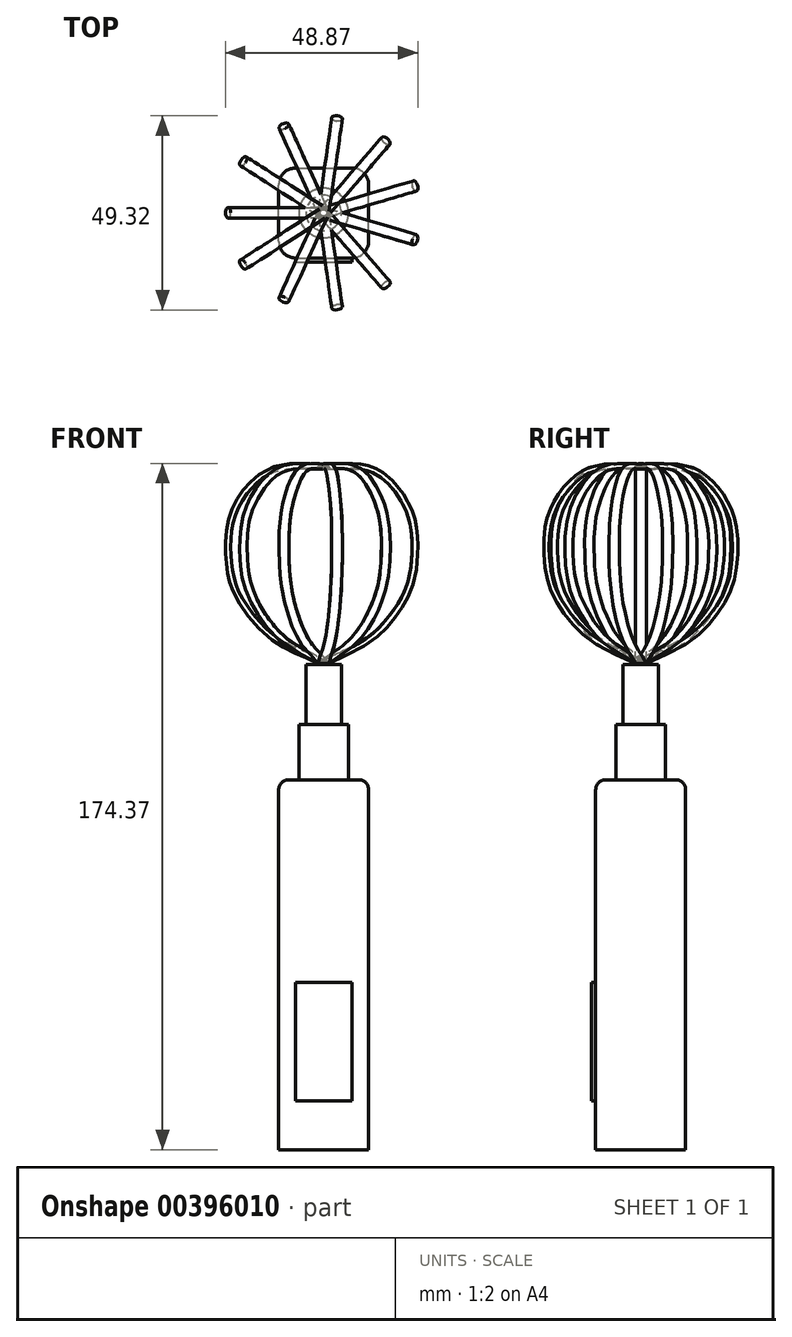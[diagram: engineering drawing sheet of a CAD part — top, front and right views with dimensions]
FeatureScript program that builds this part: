
annotation { "Feature Type Name" : "Feature", "Feature Type Description" : "" }
export const myFeature = defineFeature(function(context is Context, id is Id, definition is map)
    precondition{}
    {
        {
            var Q0;
            Q0=qCreatedBy(makeId("Front.planeOp"),FACE);
            var sketch = newSketch(context, id + "F0", { "sketchPlane" : qUnion([Q0])});
            skLineSegment(sketch, "E0", {"start": v(-13.86, -65.4) * mm, "end": v(-13.86, 28.57) * mm});
            skLineSegment(sketch, "E1", {"start": v(-13.86, 28.57) * mm, "end": v(9, 28.57) * mm});
            skLineSegment(sketch, "E2", {"start": v(9, 28.57) * mm, "end": v(9, -65.4) * mm});
            skLineSegment(sketch, "E3", {"start": v(9, -65.4) * mm, "end": v(-13.86, -65.4) * mm});
            skSolve(sketch);
        }
        {
            var Q0;
            Q0 = qSketchRegion(id + "F0", true);
            extrude(context, id + "F1", {"entities" : qUnion([Q0]), "depth" : 22.86 * mm});
        }
        {
            var Q0;
            Q0=makeQuery(id+"F1.opExtrude","CAP_EDGE",EDGE,{"disambiguationData":[OSD([sQuery(id+"F0.wireOp",EDGE,"E0")])],"isStart":true});
            var Q1;
            Q1=makeQuery(id+"F1.opExtrude","CAP_EDGE",EDGE,{"disambiguationData":[OSD([sQuery(id+"F0.wireOp",EDGE,"E0")])],"isStart":false});
            var Q2;
            Q2=makeQuery(id+"F1.opExtrude","CAP_EDGE",EDGE,{"disambiguationData":[OSD([sQuery(id+"F0.wireOp",EDGE,"E2")])],"isStart":true});
            var Q3;
            Q3=makeQuery(id+"F1.opExtrude","CAP_EDGE",EDGE,{"disambiguationData":[OSD([sQuery(id+"F0.wireOp",EDGE,"E2")])],"isStart":false});
            fillet(context, id + "F2", {"entities" : qUnion([Q0, Q1, Q2, Q3]), "radius" : 4.3 * mm, "tangentPropagation" : true, "allowEdgeOverflow" : false});
        }
        {
            var Q0;
            Q0=makeQuery(id+"F1.opExtrude","CAP_EDGE",EDGE,{"disambiguationData":[OSD([sQuery(id+"F0.wireOp",EDGE,"E1")])],"isStart":false});
            fillet(context, id + "F3", {"entities" : qUnion([Q0]), "radius" : 2.54 * mm, "tangentPropagation" : true, "allowEdgeOverflow" : false});
        }
        {
            var Q0;
            Q0=qCreatedBy(makeId("Top.planeOp"),FACE);
            cPlane(context, id + "F4", {"entities" : qUnion([Q0]), "cplaneType" : CPlaneType.OFFSET, "offset" : 28.45 * mm, "width" : 152.4 * mm, "height" : 152.4 * mm});
        }
        {
            var Q0;
            Q0=qCreatedBy(id+"F4.planeOp",FACE);
            var sketch = newSketch(context, id + "F5", { "sketchPlane" : qUnion([Q0])});
            skCircle(sketch, "E4", {"center": v(-2.43, -11.43) * mm, "radius": 6.3 * mm});
            skSolve(sketch);
        }
        {
            var Q0;
            Q0 = qSketchRegion(id + "F5", true);
            extrude(context, id + "F6", {"entities" : qUnion([Q0]), "operationType" : NewBodyOperationType.ADD, "depth" : 14.22 * mm});
        }
        {
            var Q0;
            Q0=qCreatedBy(id+"F4.planeOp",FACE);
            cPlane(context, id + "F7", {"entities" : qUnion([Q0]), "cplaneType" : CPlaneType.OFFSET, "offset" : 12.45 * mm, "width" : 152.4 * mm, "height" : 152.4 * mm});
        }
        {
            var Q0;
            Q0=qCreatedBy(id+"F7.planeOp",FACE);
            var sketch = newSketch(context, id + "F8", { "sketchPlane" : qUnion([Q0])});
            skCircle(sketch, "E5", {"center": v(-2.43, -11.43) * mm, "radius": 4.51 * mm});
            skSolve(sketch);
        }
        {
            var Q0;
            Q0 = qSketchRegion(id + "F8", true);
            extrude(context, id + "F9", {"entities" : qUnion([Q0]), "operationType" : NewBodyOperationType.ADD, "depth" : 17.02 * mm});
        }
        {
            var Q0;
            Q0=qCreatedBy(makeId("Front.planeOp"),FACE);
            cPlane(context, id + "F10", {"entities" : qUnion([Q0]), "cplaneType" : CPlaneType.OFFSET, "offset" : 23.1 * mm, "width" : 152.4 * mm, "height" : 152.4 * mm});
        }
        {
            var Q0;
            Q0=makeQuery(id+"F1.opExtrude","CAP_FACE",FACE,{"disambiguationData":[OSD([sQuery(id+"F0.wireOp",EDGE,"E0"),sQuery(id+"F0.wireOp",EDGE,"E1"),sQuery(id+"F0.wireOp",EDGE,"E2"),sQuery(id+"F0.wireOp",EDGE,"E3")])],"isStart":false});
            var sketch = newSketch(context, id + "F11", { "sketchPlane" : qUnion([Q0])});
            skLineSegment(sketch, "E6.bottom", {"start": v(-9.56, -53.07) * mm, "end": v(4.71, -53.07) * mm});
            skLineSegment(sketch, "E6.top", {"start": v(-9.56, -22.97) * mm, "end": v(4.71, -22.97) * mm});
            skLineSegment(sketch, "E6.left", {"start": v(-9.56, -53.07) * mm, "end": v(-9.56, -22.97) * mm});
            skLineSegment(sketch, "E6.right", {"start": v(4.71, -53.07) * mm, "end": v(4.71, -22.97) * mm});
            skSolve(sketch);
        }
        {
            var Q0;
            Q0=makeQuery(id+"F11.imprint","IMPRINT",FACE,{"disambiguationData":[TD([[makeQuery(id+"F11.imprint","IMPRINT",EDGE,{"derivedFrom":sQuery(id+"F11.wireOp",EDGE,"E6.bottom")}),1.0]])]});
            extrude(context, id + "F12", {"entities" : qUnion([Q0]), "operationType" : NewBodyOperationType.ADD, "depth" : 1.02 * mm});
        }
        {
            var Q0;
            Q0=makeQuery(id+"F12.opExtrude","CAP_FACE",FACE,{"disambiguationData":[OSD([sQuery(id+"F11.wireOp",EDGE,"E6.bottom"),sQuery(id+"F11.wireOp",EDGE,"E6.top"),sQuery(id+"F11.wireOp",EDGE,"E6.left"),sQuery(id+"F11.wireOp",EDGE,"E6.right")])],"isStart":false});
            var sketch = newSketch(context, id + "F13", { "sketchPlane" : qUnion([Q0])});
            skLineSegment(sketch, "E7", {"start": v(-7.14, -26.06) * mm, "end": v(2.29, -26.06) * mm});
            skSolve(sketch);
        }
        {
            var Q0;
            Q0=sQuery(id+"F13.wireOp",EDGE,"E7");
            extrude(context, id + "F14", {"bodyType" : ToolBodyType.SURFACE, "surfaceEntities" : qUnion([Q0]), "oppositeDirection" : true, "depth" : 2.03 * mm});
        }
        {
            var Q0;
            Q0=makeQuery(id+"F12.opExtrude","CAP_FACE",FACE,{"disambiguationData":[OSD([sQuery(id+"F11.wireOp",EDGE,"E6.bottom"),sQuery(id+"F11.wireOp",EDGE,"E6.top"),sQuery(id+"F11.wireOp",EDGE,"E6.left"),sQuery(id+"F11.wireOp",EDGE,"E6.right")])],"isStart":false});
            var sketch = newSketch(context, id + "F15", { "sketchPlane" : qUnion([Q0])});
            skLineSegment(sketch, "E8", {"start": v(-9.56, -48.5) * mm, "end": v(4.71, -48.5) * mm});
            skLineSegment(sketch, "E9", {"start": v(-9.56, -45.95) * mm, "end": v(4.71, -45.95) * mm});
            skLineSegment(sketch, "E10", {"start": v(-9.56, -41.38) * mm, "end": v(4.71, -41.38) * mm});
            skLineSegment(sketch, "E11", {"start": v(-9.56, -38.84) * mm, "end": v(4.71, -38.84) * mm});
            skSolve(sketch);
        }
        {
            var Q0;
            Q0=sQuery(id+"F15.wireOp",EDGE,"E8");
            extrude(context, id + "F16", {"bodyType" : ToolBodyType.SURFACE, "surfaceEntities" : qUnion([Q0]), "oppositeDirection" : true, "depth" : 5.82 * mm});
        }
        {
            var Q0;
            Q0=sQuery(id+"F15.wireOp",EDGE,"E11");
            var Q1;
            Q1=sQuery(id+"F15.wireOp",EDGE,"E10");
            var Q2;
            Q2=sQuery(id+"F15.wireOp",EDGE,"E9");
            var Q3;
            Q3=sQuery(id+"F15.wireOp",EDGE,"E8");
            extrude(context, id + "F17", {"bodyType" : ToolBodyType.SURFACE, "surfaceEntities" : qUnion([Q0, Q1, Q2, Q3]), "oppositeDirection" : true, "depth" : 9.5 * mm});
        }
        {
            var Q0;
            Q0=qCreatedBy(id+"F10.planeOp",FACE);
            cPlane(context, id + "F18", {"entities" : qUnion([Q0]), "cplaneType" : CPlaneType.OFFSET, "offset" : 11.68 * mm, "oppositeDirection" : true, "width" : 152.4 * mm, "height" : 152.4 * mm});
        }
        {
            var Q0;
            Q0=qCreatedBy(id+"F7.planeOp",FACE);
            cPlane(context, id + "F19", {"entities" : qUnion([Q0]), "cplaneType" : CPlaneType.OFFSET, "offset" : 17.02 * mm, "oppositeDirection" : true, "width" : 152.4 * mm, "height" : 152.4 * mm});
        }
        {
            var Q0;
            Q0=qCreatedBy(id+"F18.planeOp",FACE);
            var sketch = newSketch(context, id + "F20", { "sketchPlane" : qUnion([Q0])});
            skFitSpline(sketch, "E12", {"points": [v(-2.52, 58.13) * mm, v(-14.5, 64.12) * mm, v(-24.33, 75.65) * mm, v(-26.6, 85.02) * mm, v(-25.58, 95.76) * mm, v(-19.59, 104.69) * mm, v(-12.24, 108.08) * mm, v(-2.8, 108.12) * mm], "startDerivative": vector(-79.34, 44.57) * mm, "endDerivative": vector(49.51, -0.45) * mm});
            skSolve(sketch);
        }
        {
            var Q0;
            Q0=makeQuery(id+"F9.opExtrude","CAP_FACE",FACE,{"disambiguationData":[OSD([sQuery(id+"F8.wireOp",EDGE,"E5")])],"isStart":false});
            cPlane(context, id + "F21", {"entities" : qUnion([Q0]), "cplaneType" : CPlaneType.OFFSET, "offset" : 0.2 * mm, "width" : 152.4 * mm, "height" : 152.4 * mm});
        }
        {
            var Q0;
            Q0=qCreatedBy(id+"F21.planeOp",FACE);
            var sketch = newSketch(context, id + "F22", { "sketchPlane" : qUnion([Q0])});
            skCircle(sketch, "E13", {"center": v(-2.49, -11.38) * mm, "radius": 1.36 * mm});
            skSolve(sketch);
        }
        {
            var Q0;
            Q0=makeQuery(id+"F22.imprint","IMPRINT",FACE,{"disambiguationData":[TD([[makeQuery(id+"F22.imprint","IMPRINT",EDGE,{"derivedFrom":sQuery(id+"F22.wireOp",EDGE,"E13")}),1.0]])]});
            var Q1;
            Q1=sQuery(id+"F20.wireOp",EDGE,"E12");
            sweep(context, id + "F23", {"profiles" : qUnion([Q0]), "path" : qUnion([Q1])});
        }
        {
            var Q0;
            Q0=makeQuery(id+"F23.opSweep","SWEPT_BODY",BODY,{"disambiguationData":[OSD([sQuery(id+"F20.wireOp",EDGE,"E12"),sQuery(id+"F22.wireOp",EDGE,"E13")])]});
            var Q1;
            Q1=makeQuery(id+"F23.opSweep","CAP_EDGE",EDGE,{"disambiguationData":[OSD([sQuery(id+"F20.wireOp",VERTEX,"E12.start"),sQuery(id+"F22.wireOp",EDGE,"E13")])],"isStart":true});
            circularPattern(context, id + "F24", {"entities" : qUnion([Q0]), "axis" : qUnion([Q1]), "angle" : 360 * degree, "instanceCount" : 11, "equalSpace" : true});
        }
    });
